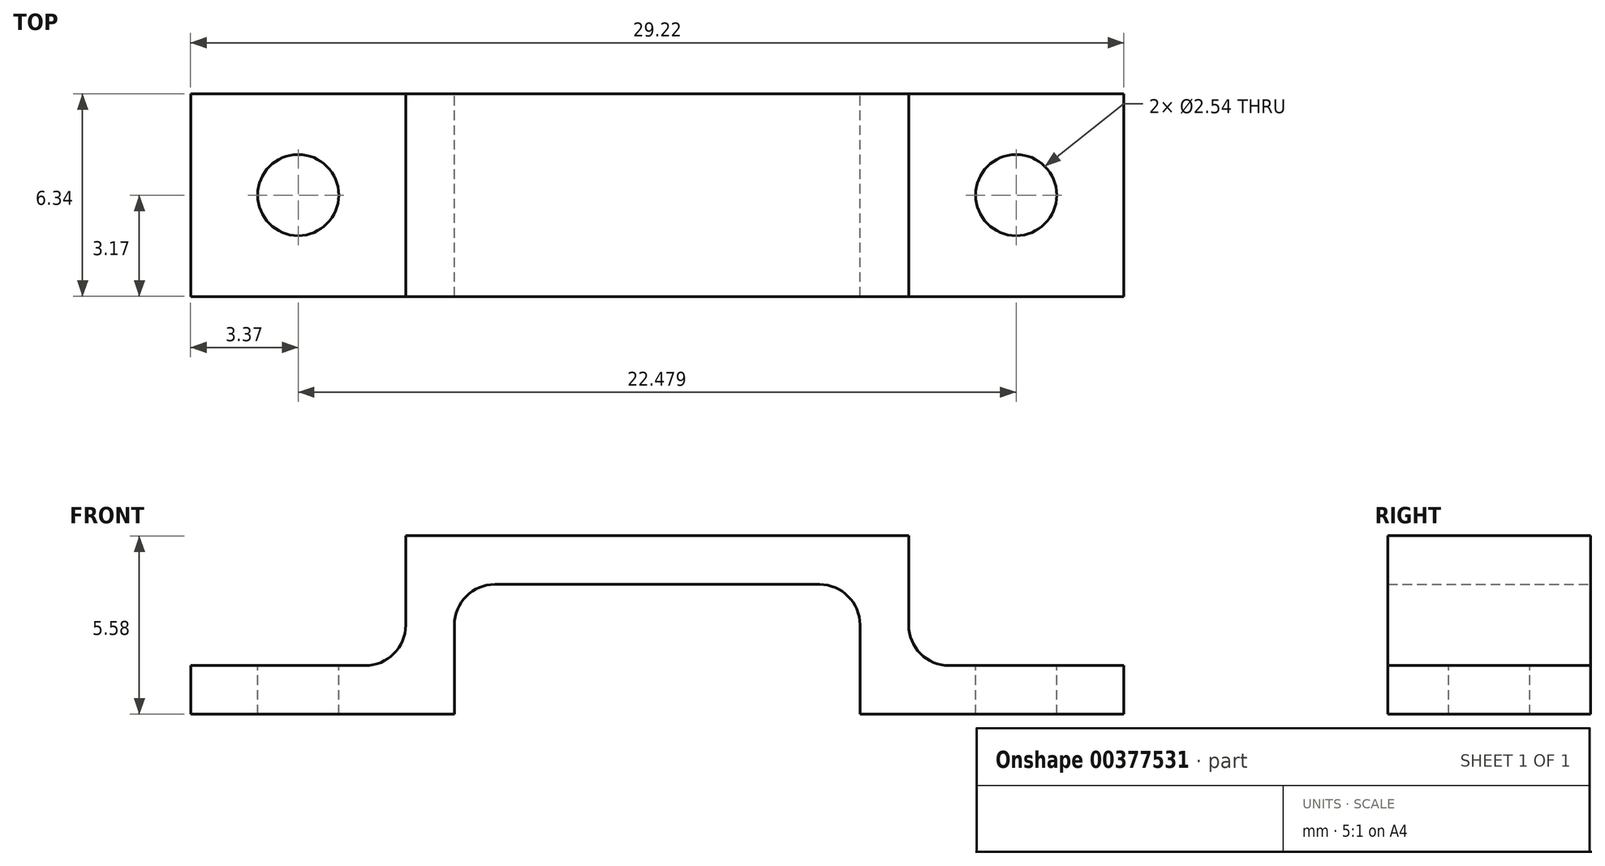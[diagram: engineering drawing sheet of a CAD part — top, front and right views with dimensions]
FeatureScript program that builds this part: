
annotation { "Feature Type Name" : "Feature", "Feature Type Description" : "" }
export const myFeature = defineFeature(function(context is Context, id is Id, definition is map)
    precondition{}
    {
        {
            var Q0;
            Q0=qCreatedBy(makeId("Front.planeOp"),FACE);
            var sketch = newSketch(context, id + "F0", { "sketchPlane" : qUnion([Q0])});
            skLineSegment(sketch, "E0", {"start": v(-6.35, -4.06) * mm, "end": v(-6.35, 0) * mm});
            skLineSegment(sketch, "E1", {"start": v(-6.35, 0) * mm, "end": v(6.35, 0) * mm});
            skLineSegment(sketch, "E2", {"start": v(6.35, 0) * mm, "end": v(6.35, -4.06) * mm});
            skLineSegment(sketch, "E3", {"start": v(6.35, -4.06) * mm, "end": v(14.6, -4.06) * mm});
            skLineSegment(sketch, "E4", {"start": v(-14.6, -4.06) * mm, "end": v(-6.35, -4.06) * mm});
            skLineSegment(sketch, "E5.0", {"start": v(7.87, -2.54) * mm, "end": v(14.6, -2.54) * mm});
            skLineSegment(sketch, "E5.1", {"start": v(-14.6, -2.54) * mm, "end": v(-7.87, -2.54) * mm});
            skLineSegment(sketch, "E5.2", {"start": v(-7.87, -2.54) * mm, "end": v(-7.87, 1.52) * mm});
            skLineSegment(sketch, "E5.3", {"start": v(-7.87, 1.52) * mm, "end": v(7.87, 1.52) * mm});
            skLineSegment(sketch, "E5.4", {"start": v(7.87, 1.52) * mm, "end": v(7.87, -2.54) * mm});
            skLineSegment(sketch, "E6", {"start": v(-14.6, -2.54) * mm, "end": v(-14.6, -4.06) * mm});
            skLineSegment(sketch, "E7", {"start": v(14.6, -2.54) * mm, "end": v(14.6, -4.06) * mm});
            skSolve(sketch);
        }
        {
            var Q0;
            Q0=makeQuery(id+"F0.imprint","IMPRINT",FACE,{"disambiguationData":[TD([[makeQuery(id+"F0.imprint","IMPRINT",EDGE,{"derivedFrom":sQuery(id+"F0.wireOp",EDGE,"E0")}),1.0]])]});
            extrude(context, id + "F1", {"entities" : qUnion([Q0]), "endBound" : BoundingType.SYMMETRIC, "depth" : 6.35 * mm});
        }
        {
            var Q0;
            Q0=makeQuery(id+"F1.opExtrude","SWEPT_FACE",FACE,{"disambiguationData":[OSD([sQuery(id+"F0.wireOp",EDGE,"E5.0")])]});
            var sketch = newSketch(context, id + "F2", { "sketchPlane" : qUnion([Q0])});
            skCircle(sketch, "E8", {"center": v(-11.24, 0) * mm, "radius": 1.27 * mm});
            skCircle(sketch, "E9", {"center": v(11.24, 0) * mm, "radius": 1.27 * mm});
            skSolve(sketch);
        }
        {
            var Q0;
            Q0=makeQuery(id+"F2.imprint","IMPRINT",FACE,{"disambiguationData":[TD([[makeQuery(id+"F2.imprint","IMPRINT",EDGE,{"derivedFrom":sQuery(id+"F2.wireOp",EDGE,"E8")}),1.0]])]});
            var Q1;
            Q1=makeQuery(id+"F2.imprint","IMPRINT",FACE,{"disambiguationData":[TD([[makeQuery(id+"F2.imprint","IMPRINT",EDGE,{"derivedFrom":sQuery(id+"F2.wireOp",EDGE,"E9")}),1.0]])]});
            extrude(context, id + "F3", {"entities" : qUnion([Q0, Q1]), "operationType" : NewBodyOperationType.REMOVE, "endBound" : BoundingType.UP_TO_NEXT, "oppositeDirection" : true, "depth" : 25.4 * mm});
        }
        {
            var Q0;
            Q0=makeQuery(id+"F1.opExtrude","SWEPT_EDGE",EDGE,{"disambiguationData":[OSD([sQuery(id+"F0.wireOp",EDGE,"E0"),sQuery(id+"F0.wireOp",EDGE,"E1")])]});
            var Q1;
            Q1=makeQuery(id+"F1.opExtrude","SWEPT_EDGE",EDGE,{"disambiguationData":[OSD([sQuery(id+"F0.wireOp",EDGE,"E1"),sQuery(id+"F0.wireOp",EDGE,"E2")])]});
            var Q2;
            Q2=makeQuery(id+"F1.opExtrude","SWEPT_EDGE",EDGE,{"disambiguationData":[OSD([sQuery(id+"F0.wireOp",EDGE,"E5.1"),sQuery(id+"F0.wireOp",EDGE,"E5.2")])]});
            var Q3;
            Q3=makeQuery(id+"F1.opExtrude","SWEPT_EDGE",EDGE,{"disambiguationData":[OSD([sQuery(id+"F0.wireOp",EDGE,"E5.0"),sQuery(id+"F0.wireOp",EDGE,"E5.4")])]});
            fillet(context, id + "F4", {"entities" : qUnion([Q0, Q1, Q2, Q3]), "radius" : 1.27 * mm, "tangentPropagation" : true, "allowEdgeOverflow" : false});
        }
    });
